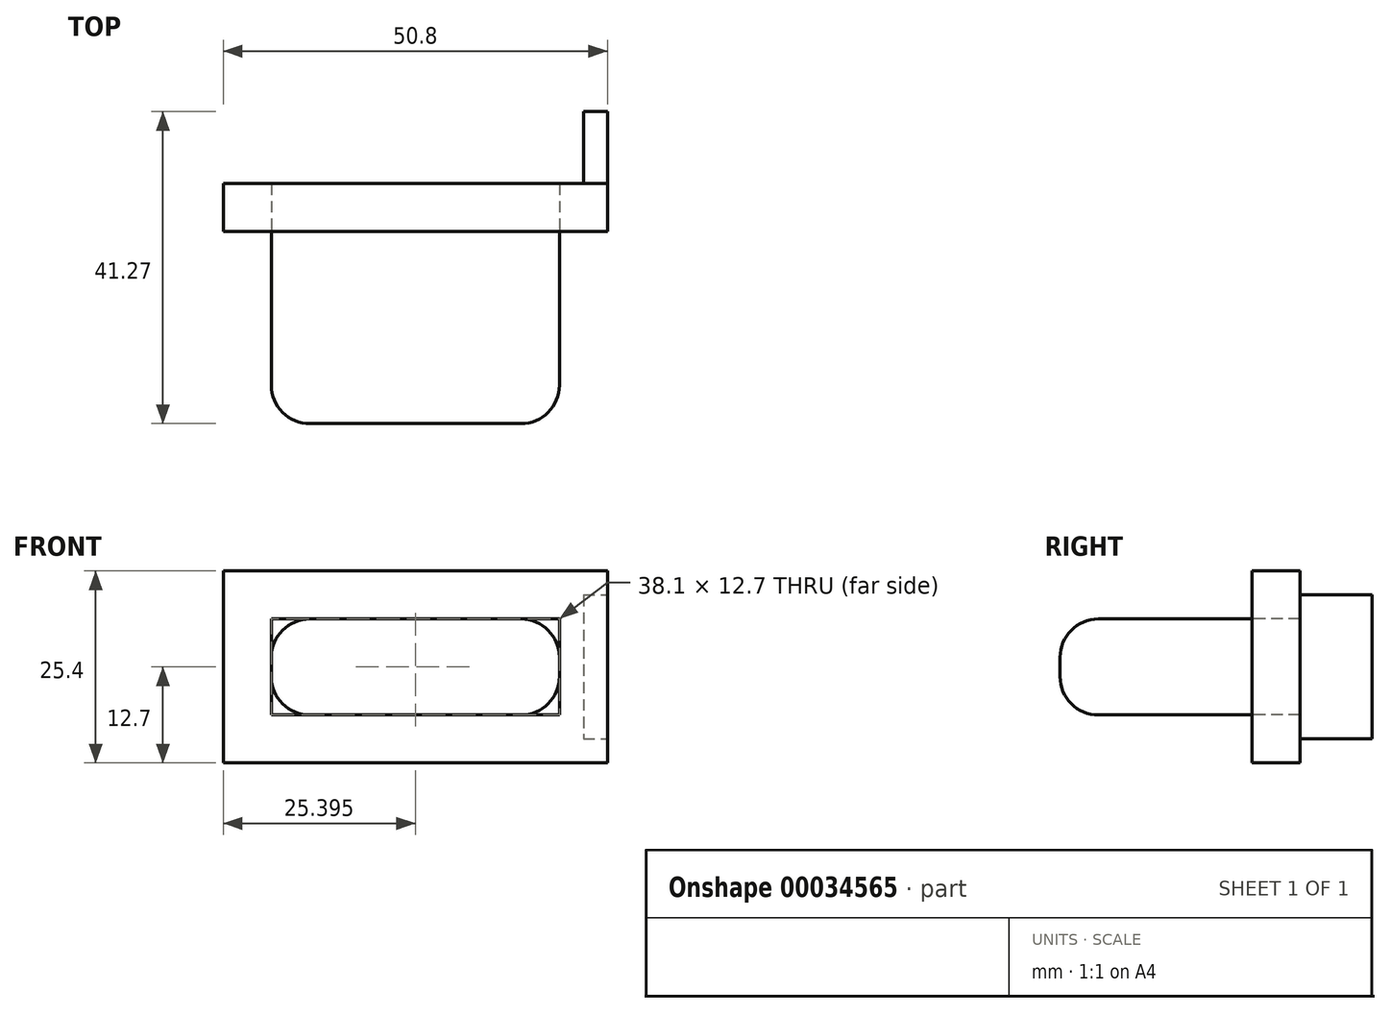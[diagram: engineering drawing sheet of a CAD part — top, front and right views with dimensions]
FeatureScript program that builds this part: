
annotation { "Feature Type Name" : "Feature", "Feature Type Description" : "" }
export const myFeature = defineFeature(function(context is Context, id is Id, definition is map)
    precondition{}
    {
        {
            var Q0;
            Q0=qCreatedBy(makeId("Front.planeOp"),FACE);
            var sketch = newSketch(context, id + "F0", { "sketchPlane" : qUnion([Q0])});
            skLineSegment(sketch, "E0.bottom", {"start": v(-20.46, 3.81) * mm, "end": v(17.64, 3.81) * mm});
            skLineSegment(sketch, "E0.top", {"start": v(-20.46, -8.89) * mm, "end": v(17.64, -8.89) * mm});
            skLineSegment(sketch, "E0.left", {"start": v(-20.46, 3.81) * mm, "end": v(-20.46, -8.89) * mm});
            skLineSegment(sketch, "E0.right", {"start": v(17.64, 3.81) * mm, "end": v(17.64, -8.89) * mm});
            skSolve(sketch);
        }
        {
            var Q0;
            Q0 = qSketchRegion(id + "F0", true);
            extrude(context, id + "F1", {"entities" : qUnion([Q0]), "oppositeDirection" : true, "depth" : 25.4 * mm});
        }
        {
            var Q0;
            Q0=makeQuery(id+"F1.opExtrude","CAP_FACE",FACE,{"disambiguationData":[OSD([sQuery(id+"F0.wireOp",EDGE,"E0.bottom"),sQuery(id+"F0.wireOp",EDGE,"E0.top"),sQuery(id+"F0.wireOp",EDGE,"E0.left"),sQuery(id+"F0.wireOp",EDGE,"E0.right")])],"isStart":false});
            var sketch = newSketch(context, id + "F2", { "sketchPlane" : qUnion([Q0])});
            skLineSegment(sketch, "E1.bottom", {"start": v(-23.99, 10.16) * mm, "end": v(26.81, 10.16) * mm});
            skLineSegment(sketch, "E1.top", {"start": v(-23.99, -15.24) * mm, "end": v(26.81, -15.24) * mm});
            skLineSegment(sketch, "E1.left", {"start": v(-23.99, 10.16) * mm, "end": v(-23.99, -15.24) * mm});
            skLineSegment(sketch, "E1.right", {"start": v(26.81, 10.16) * mm, "end": v(26.81, -15.24) * mm});
            skSolve(sketch);
        }
        {
            var Q0;
            Q0=makeQuery(id+"F2.imprint","IMPRINT",FACE,{"disambiguationData":[TD([[makeQuery(id+"F2.imprint","IMPRINT",EDGE,{"derivedFrom":sQuery(id+"F2.wireOp",EDGE,"E1.bottom")}),-1.0]])]});
            extrude(context, id + "F3", {"entities" : qUnion([Q0]), "depth" : 6.35 * mm});
        }
        {
            var Q0;
            Q0=makeQuery(id+"F3.opExtrude","SWEPT_FACE",FACE,{"disambiguationData":[OSD([sQuery(id+"F2.wireOp",EDGE,"E1.left")])]});
            var sketch = newSketch(context, id + "F4", { "sketchPlane" : qUnion([Q0])});
            skLineSegment(sketch, "E2.bottom", {"start": v(31.75, 6.99) * mm, "end": v(41.27, 6.99) * mm});
            skLineSegment(sketch, "E2.top", {"start": v(31.75, -12.06) * mm, "end": v(41.27, -12.06) * mm});
            skLineSegment(sketch, "E2.left", {"start": v(31.75, 6.99) * mm, "end": v(31.75, -12.06) * mm});
            skLineSegment(sketch, "E2.right", {"start": v(41.27, 6.99) * mm, "end": v(41.27, -12.06) * mm});
            skSolve(sketch);
        }
        {
            var Q0;
            Q0=makeQuery(id+"F4.imprint","IMPRINT",FACE,{"disambiguationData":[TD([[makeQuery(id+"F4.imprint","IMPRINT",EDGE,{"derivedFrom":sQuery(id+"F4.wireOp",EDGE,"E2.bottom")}),-1.0]])]});
            extrude(context, id + "F5", {"entities" : qUnion([Q0]), "oppositeDirection" : true, "depth" : 3.17 * mm});
        }
        {
            var Q0;
            Q0=makeQuery(id+"F1.opExtrude","SWEPT_EDGE",EDGE,{"disambiguationData":[OSD([sQuery(id+"F0.wireOp",EDGE,"E0.bottom"),sQuery(id+"F0.wireOp",EDGE,"E0.right")])]});
            var Q1;
            Q1=makeQuery(id+"F1.opExtrude","SWEPT_EDGE",EDGE,{"disambiguationData":[OSD([sQuery(id+"F0.wireOp",EDGE,"E0.top"),sQuery(id+"F0.wireOp",EDGE,"E0.right")])]});
            var Q2;
            Q2=makeQuery(id+"F1.opExtrude","CAP_EDGE",EDGE,{"disambiguationData":[OSD([sQuery(id+"F0.wireOp",EDGE,"E0.right")])],"isStart":true});
            var Q3;
            Q3=makeQuery(id+"F1.opExtrude","CAP_EDGE",EDGE,{"disambiguationData":[OSD([sQuery(id+"F0.wireOp",EDGE,"E0.bottom")])],"isStart":true});
            var Q4;
            Q4=makeQuery(id+"F1.opExtrude","CAP_EDGE",EDGE,{"disambiguationData":[OSD([sQuery(id+"F0.wireOp",EDGE,"E0.top")])],"isStart":true});
            var Q5;
            Q5=makeQuery(id+"F1.opExtrude","CAP_EDGE",EDGE,{"disambiguationData":[OSD([sQuery(id+"F0.wireOp",EDGE,"E0.left")])],"isStart":true});
            var Q6;
            Q6=makeQuery(id+"F1.opExtrude","SWEPT_EDGE",EDGE,{"disambiguationData":[OSD([sQuery(id+"F0.wireOp",EDGE,"E0.bottom"),sQuery(id+"F0.wireOp",EDGE,"E0.left")])]});
            var Q7;
            Q7=makeQuery(id+"F1.opExtrude","SWEPT_EDGE",EDGE,{"disambiguationData":[OSD([sQuery(id+"F0.wireOp",EDGE,"E0.top"),sQuery(id+"F0.wireOp",EDGE,"E0.left")])]});
            fillet(context, id + "F6", {"entities" : qUnion([Q0, Q1, Q2, Q3, Q4, Q5, Q6, Q7]), "radius" : 5.08 * mm, "tangentPropagation" : true, "allowEdgeOverflow" : false});
        }
    });
